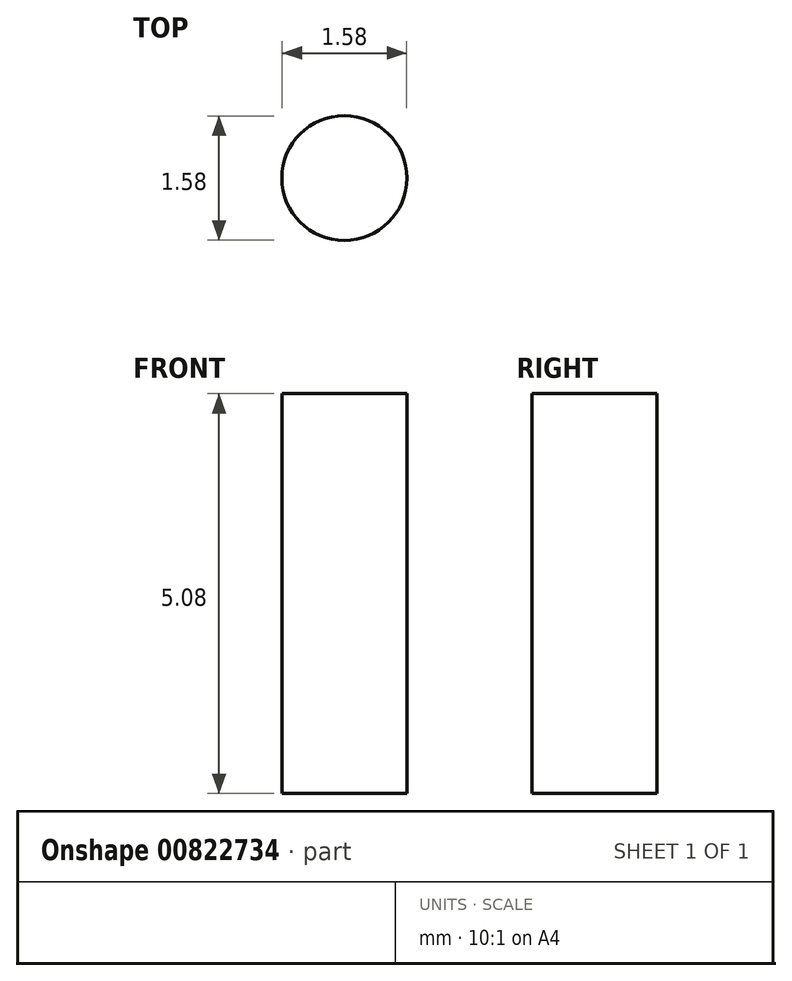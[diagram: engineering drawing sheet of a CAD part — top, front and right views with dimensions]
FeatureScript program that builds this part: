
annotation { "Feature Type Name" : "Feature", "Feature Type Description" : "" }
export const myFeature = defineFeature(function(context is Context, id is Id, definition is map)
    precondition{}
    {
        {
            var Q0;
            Q0=qCreatedBy(makeId("Top.planeOp"),FACE);
            var sketch = newSketch(context, id + "F0", { "sketchPlane" : qUnion([Q0])});
            skCircle(sketch, "E0", {"center": v(0, 0) * mm, "radius": 0.8 * mm});
            skSolve(sketch);
        }
        {
            var Q0;
            Q0=makeQuery(id+"F0.imprint","IMPRINT",FACE,{"disambiguationData":[TD([[makeQuery(id+"F0.imprint","IMPRINT",EDGE,{"derivedFrom":sQuery(id+"F0.wireOp",EDGE,"E0")}),1.0]])]});
            extrude(context, id + "F1", {"entities" : qUnion([Q0]), "depth" : 5.08 * mm, "offsetDistance" : 25.4 * mm});
        }
    });
